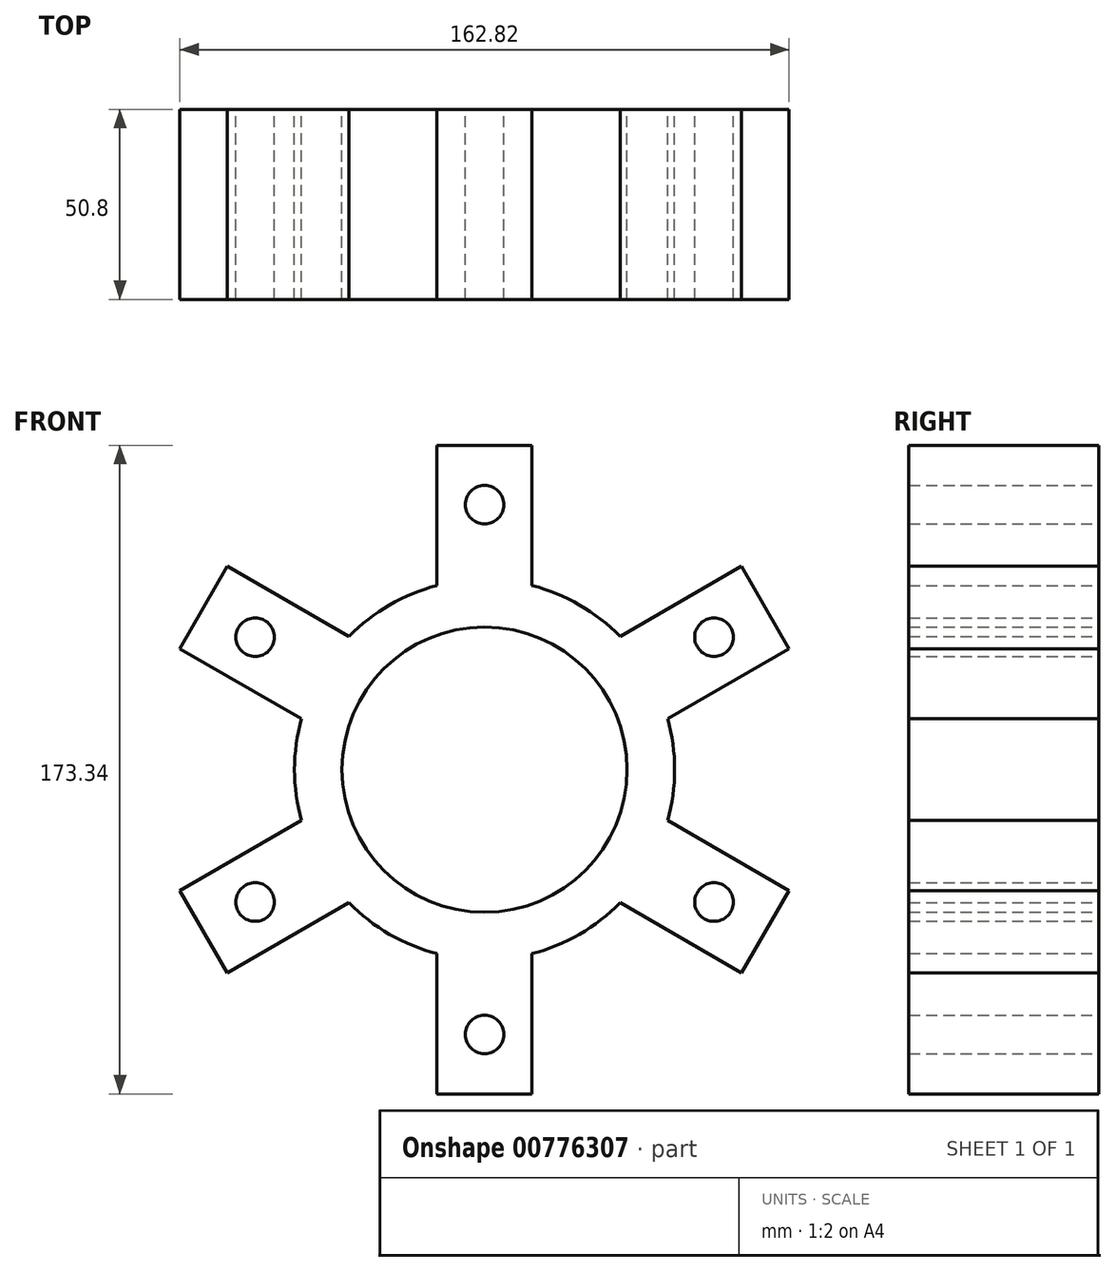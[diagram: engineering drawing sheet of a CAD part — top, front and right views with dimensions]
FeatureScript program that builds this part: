
annotation { "Feature Type Name" : "Feature", "Feature Type Description" : "" }
export const myFeature = defineFeature(function(context is Context, id is Id, definition is map)
    precondition{}
    {
        {
            var Q0;
            Q0=qCreatedBy(makeId("Front.planeOp"),FACE);
            var sketch = newSketch(context, id + "F0", { "sketchPlane" : qUnion([Q0])});
            skCircle(sketch, "E0", {"center": v(0, 0) * mm, "radius": 50.8 * mm});
            skCircle(sketch, "E1", {"center": v(0, 0) * mm, "radius": 38.1 * mm});
            skLineSegment(sketch, "E2", {"start": v(-12.7, 86.67) * mm, "end": v(-12.7, 49.19) * mm});
            skLineSegment(sketch, "E3", {"start": v(12.7, 49.19) * mm, "end": v(12.7, 86.67) * mm});
            skLineSegment(sketch, "E4", {"start": v(12.7, 86.67) * mm, "end": v(-12.7, 86.67) * mm});
            skLineSegment(sketch, "E5", {"start": v(-12.7, 86.67) * mm, "end": v(0, 86.67) * mm});
            skLineSegment(sketch, "E6", {"start": v(0, 86.67) * mm, "end": v(0, 70.8) * mm});
            skCircle(sketch, "E7", {"center": v(0, 70.8) * mm, "radius": 5.15 * mm});
            skSolve(sketch);
        }
        {
            var Q0;
            Q0 = qSketchRegion(id + "F0", true);
            extrude(context, id + "F1", {"entities" : qUnion([Q0]), "endBound" : BoundingType.SYMMETRIC, "depth" : 50.8 * mm, "offsetDistance" : 25.4 * mm});
        }
        {
            var Q0;
            Q0=makeQuery(id+"F1.opExtrude","SWEPT_FACE",FACE,{"disambiguationData":[OSD([sQuery(id+"F0.wireOp",EDGE,"E3")])]});
            var Q1;
            Q1=makeQuery(id+"F1.opExtrude","SWEPT_FACE",FACE,{"disambiguationData":[OSD([sQuery(id+"F0.wireOp",EDGE,"E4"),sQuery(id+"F0.wireOp",EDGE,"E5")])]});
            var Q2;
            Q2=makeQuery(id+"F1.opExtrude","SWEPT_FACE",FACE,{"disambiguationData":[OSD([sQuery(id+"F0.wireOp",EDGE,"E2")])]});
            var Q3;
            Q3=makeQuery(id+"F1.opExtrude","SWEPT_FACE",FACE,{"disambiguationData":[OSD([sQuery(id+"F0.wireOp",EDGE,"E7")])]});
            var Q4;
            Q4=makeQuery(id+"F1.opExtrude","SWEPT_FACE",FACE,{"disambiguationData":[OSD([sQuery(id+"F0.wireOp",EDGE,"E0")])]});
            circularPattern(context, id + "F2", {"patternType" : PatternType.FACE, "faces" : qUnion([Q0, Q1, Q2, Q3]), "axis" : qUnion([Q4]), "angle" : 360 * degree, "instanceCount" : 6, "equalSpace" : true});
        }
    });
